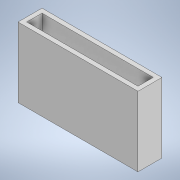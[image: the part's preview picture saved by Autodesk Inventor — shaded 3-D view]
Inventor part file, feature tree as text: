
AUTODESK INVENTOR PART (.ipt)
format: ipt  version: 2022.1 (Build 261234000, 234)  size: 96,256 bytes
history: native  units: in
note: dims shown in document units (in); Inventor stores cm internally (conversion verified against a paired STEP export)
features: extrude x1, sketch x1
ambient origin geometry x8: Origin, YZ Plane, XZ Plane, XY Plane, X Axis, Y Axis, Z Axis, Center Point
bodies: Solid1 (feature_tree)
feature tree (2):
  extrude  "Extrusion1"  Depth=3.4375in
  sketch  "Sketch1"  dims[d0=0.6875in d1=3.4375in d2=0.125in d3=0.125in d4=2.0in d5=0.0in]
